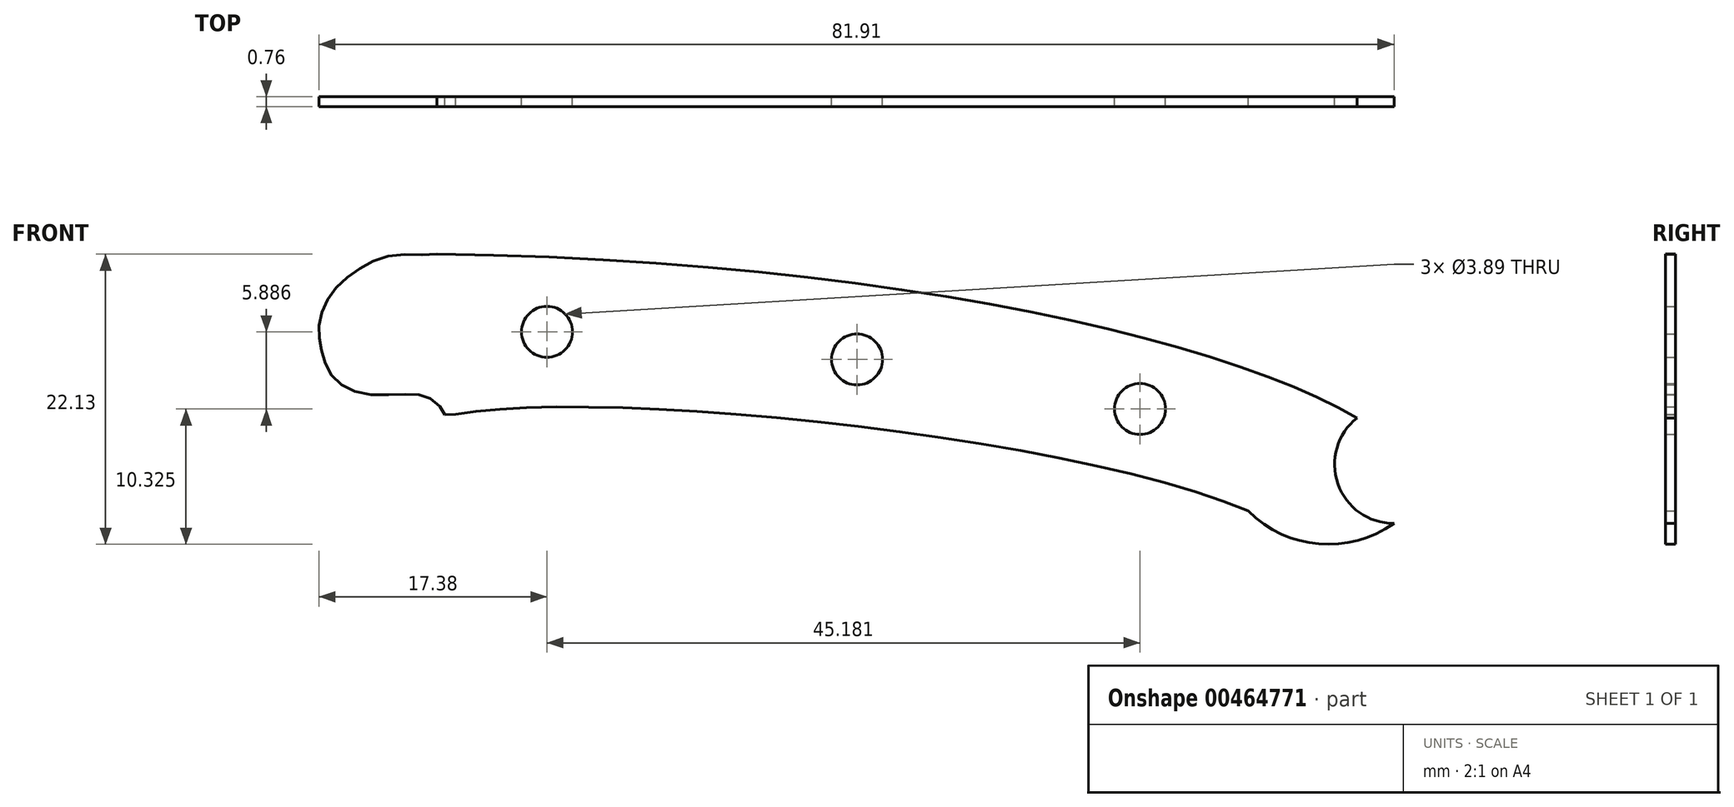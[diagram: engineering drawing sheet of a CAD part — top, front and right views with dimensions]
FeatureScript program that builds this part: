
annotation { "Feature Type Name" : "Feature", "Feature Type Description" : "" }
export const myFeature = defineFeature(function(context is Context, id is Id, definition is map)
    precondition{}
    {
        {
            var Q0;
            Q0=qCreatedBy(makeId("Front.planeOp"),FACE);
            var sketch = newSketch(context, id + "F0", { "sketchPlane" : qUnion([Q0])});
            skPoint(sketch, "E0", {"position": v(37.7, 34.47) * mm});
            skFitSpline(sketch, "E1", {"points": [v(7.11, 24.48) * mm, v(67.5, 17.12) * mm], "startDerivative": vector(32.5, 6.07) * mm, "endDerivative": vector(41.2, -17.48) * mm});
            skPoint(sketch, "E2", {"position": v(37.7, 23.57) * mm});
            skArc(sketch, "E3", {"start": v(67.5, 17.12) * mm, "mid": v(73.61, 14.57) * mm, "end": v(79.71, 17.12) * mm});
            skCircle(sketch, "E4", {"center": v(76.86, 19.24) * mm, "radius": 1.72 * mm});
            skCircle(sketch, "E5", {"center": v(14.07, 30.78) * mm, "radius": 1.94 * mm});
            skCircle(sketch, "E6", {"center": v(37.7, 28.68) * mm, "radius": 1.94 * mm});
            skCircle(sketch, "E7", {"center": v(59.25, 24.9) * mm, "radius": 1.94 * mm});
            skPoint(sketch, "E8", {"position": v(14.07, 36.48) * mm});
            skPoint(sketch, "E9", {"position": v(41.42, 33.95) * mm});
            skPoint(sketch, "E10", {"position": v(59.25, 30.4) * mm});
            skFitSpline(sketch, "E11", {"points": [v(5.7, 36.7) * mm, v(2.38, 36.62) * mm, v(-0.4, 35.48) * mm, v(-2.43, 33.6) * mm, v(-3.28, 31.36) * mm, v(-3.14, 29.43) * mm, v(-2.3, 27.4) * mm, v(0, 26.08) * mm, v(3.52, 26.03) * mm, v(5.36, 25.57) * mm, v(6.3, 24.46) * mm], "startDerivative": vector(-24.15, -3.51) * mm, "endDerivative": vector(1.15, -12.96) * mm});
            skFitSpline(sketch, "E12.trimOffspring", {"points": [v(-69.47, 27.87) * mm, v(79.71, 17.12) * mm], "startDerivative": vector(238.36, 61.55) * mm, "endDerivative": vector(-26.8, -33.68) * mm});
            skCircle(sketch, "E13", {"center": v(78.58, 20.67) * mm, "radius": 4.5 * mm});
            skLineSegment(sketch, "E14", {"start": v(7.11, 24.48) * mm, "end": v(6.3, 24.46) * mm});
            skSolve(sketch);
        }
        {
            var Q0;
            {var subQ1=sQuery(id+"F0.wireOp",EDGE,"E1");Q0=makeQuery(id+"F0.imprint","IMPRINT",FACE,{"disambiguationData":[TD([[makeQuery(id+"F0.imprint","IMPRINT",EDGE,{"derivedFrom":subQ1}),1.0]])]});}
            extrude(context, id + "F1", {"entities" : qUnion([Q0]), "depth" : 0.76 * mm});
        }
    });
